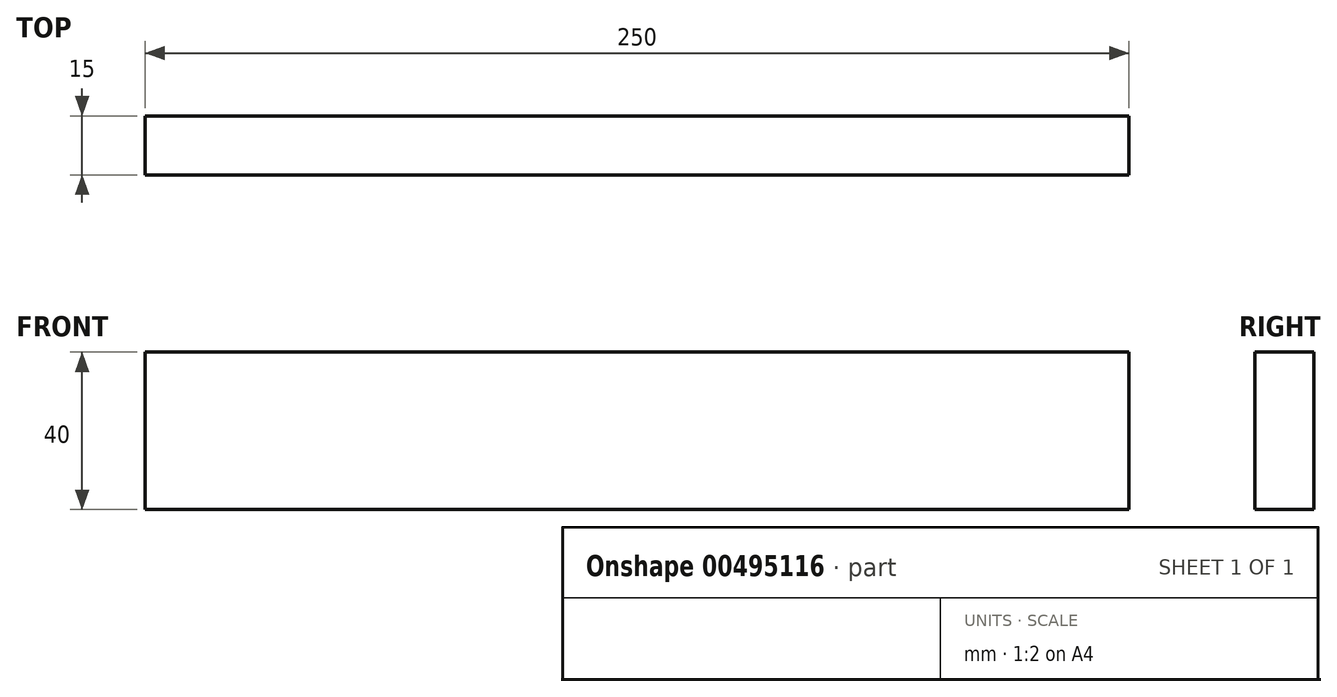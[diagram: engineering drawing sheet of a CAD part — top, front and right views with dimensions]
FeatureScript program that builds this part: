
annotation { "Feature Type Name" : "Feature", "Feature Type Description" : "" }
export const myFeature = defineFeature(function(context is Context, id is Id, definition is map)
    precondition{}
    {
        {
            var Q0;
            Q0=qCreatedBy(makeId("Front.planeOp"),FACE);
            var sketch = newSketch(context, id + "F0", { "sketchPlane" : qUnion([Q0])});
            skLineSegment(sketch, "E0.bottom", {"start": v(0, 0) * mm, "end": v(-250, 0) * mm});
            skLineSegment(sketch, "E0.top", {"start": v(0, 40) * mm, "end": v(-250, 40) * mm});
            skLineSegment(sketch, "E0.left", {"start": v(0, 0) * mm, "end": v(0, 40) * mm});
            skLineSegment(sketch, "E0.right", {"start": v(-250, 0) * mm, "end": v(-250, 40) * mm});
            skSolve(sketch);
        }
        {
            var Q0;
            Q0=makeQuery(id+"F0.imprint","IMPRINT",FACE,{"disambiguationData":[TD([[makeQuery(id+"F0.imprint","IMPRINT",EDGE,{"derivedFrom":sQuery(id+"F0.wireOp",EDGE,"E0.bottom")}),-1.0]])]});
            extrude(context, id + "F1", {"entities" : qUnion([Q0]), "depth" : 15 * mm});
        }
    });
